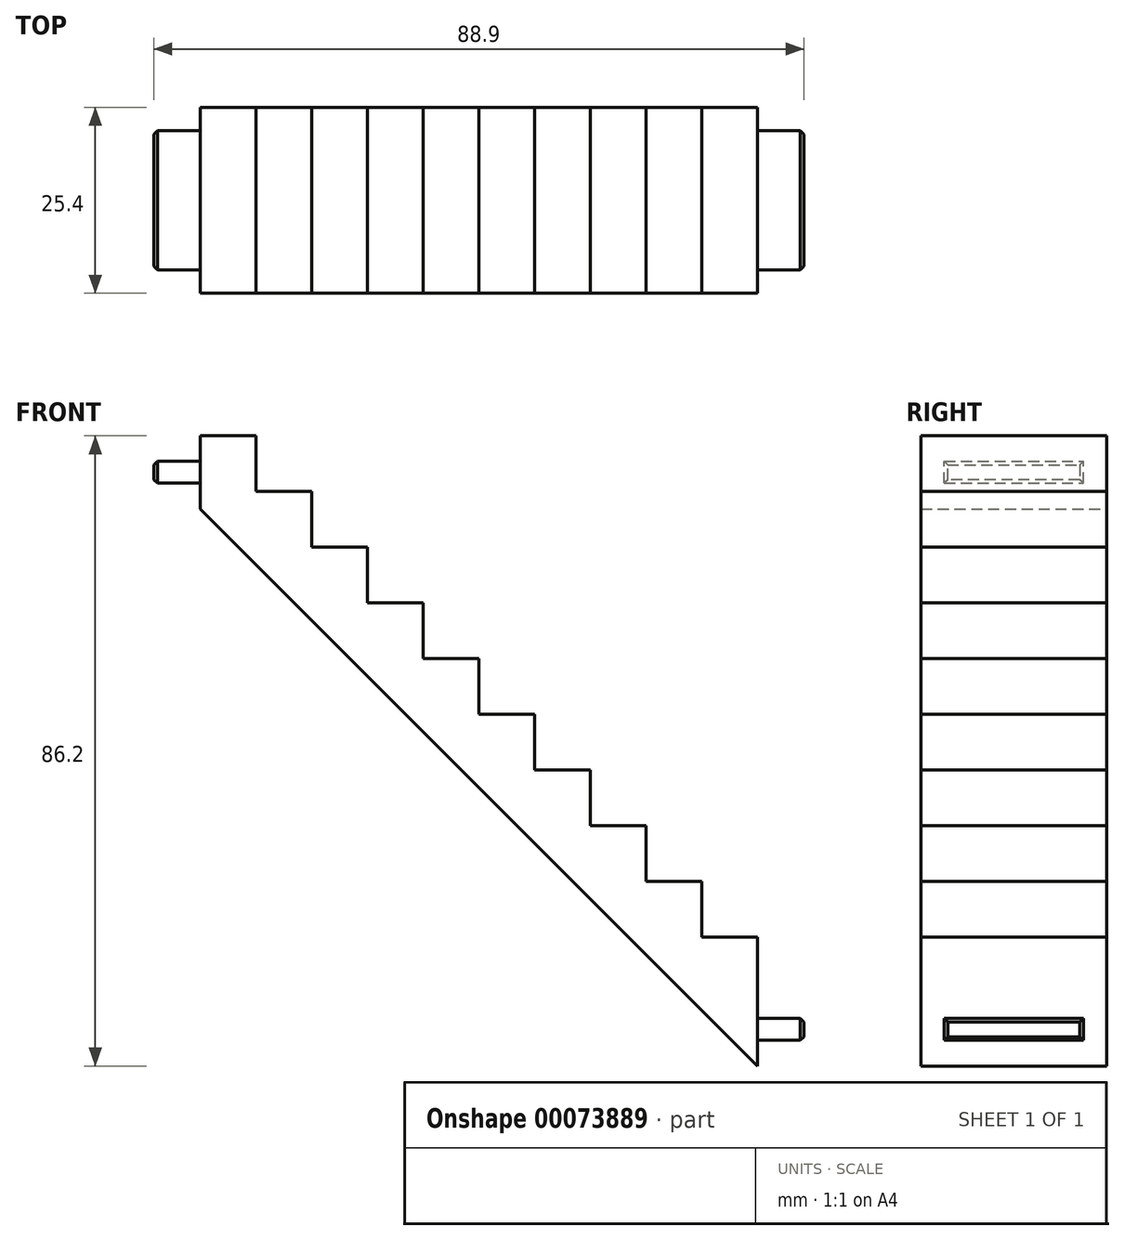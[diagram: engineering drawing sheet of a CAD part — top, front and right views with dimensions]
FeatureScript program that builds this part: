
annotation { "Feature Type Name" : "Feature", "Feature Type Description" : "" }
export const myFeature = defineFeature(function(context is Context, id is Id, definition is map)
    precondition{}
    {
        {
            var Q0;
            Q0=qCreatedBy(makeId("Front.planeOp"),FACE);
            var sketch = newSketch(context, id + "F0", { "sketchPlane" : qUnion([Q0])});
            skLineSegment(sketch, "E0.bottom", {"start": v(0, 0) * mm, "end": v(-76.2, 0) * mm, "construction": true});
            skLineSegment(sketch, "E0.top", {"start": v(0, 76.2) * mm, "end": v(-76.2, 76.2) * mm, "construction": true});
            skLineSegment(sketch, "E0.left", {"start": v(0, 0) * mm, "end": v(0, 76.2) * mm, "construction": true});
            skLineSegment(sketch, "E0.right", {"start": v(-76.2, 0) * mm, "end": v(-76.2, 76.2) * mm, "construction": true});
            skLineSegment(sketch, "E1", {"start": v(-76.2, 76.2) * mm, "end": v(0, 0) * mm, "construction": true});
            skLineSegment(sketch, "E2", {"start": v(0, 0) * mm, "end": v(0, -10) * mm});
            skLineSegment(sketch, "E3", {"start": v(-76.2, 76.2) * mm, "end": v(-76.2, 66.2) * mm});
            skLineSegment(sketch, "E4", {"start": v(-76.2, 66.2) * mm, "end": v(0, -10) * mm});
            skLineSegment(sketch, "E5", {"start": v(0, -10) * mm, "end": v(0, 0) * mm});
            skLineSegment(sketch, "E6", {"start": v(0, 0) * mm, "end": v(0, 7.62) * mm});
            skLineSegment(sketch, "E7", {"start": v(0, 7.62) * mm, "end": v(-7.62, 7.62) * mm});
            skLineSegment(sketch, "E8", {"start": v(-7.62, 7.62) * mm, "end": v(-7.62, 15.24) * mm});
            skLineSegment(sketch, "E9", {"start": v(-7.62, 15.24) * mm, "end": v(-15.24, 15.24) * mm});
            skLineSegment(sketch, "E10", {"start": v(-15.24, 15.24) * mm, "end": v(-15.24, 22.86) * mm});
            skLineSegment(sketch, "E11", {"start": v(-15.24, 22.86) * mm, "end": v(-22.86, 22.86) * mm});
            skLineSegment(sketch, "E12", {"start": v(-22.86, 22.86) * mm, "end": v(-22.86, 30.48) * mm});
            skLineSegment(sketch, "E13", {"start": v(-22.86, 30.48) * mm, "end": v(-30.48, 30.48) * mm});
            skLineSegment(sketch, "E14", {"start": v(-30.48, 30.48) * mm, "end": v(-30.48, 38.1) * mm});
            skLineSegment(sketch, "E15", {"start": v(-30.48, 38.1) * mm, "end": v(-38.1, 38.1) * mm});
            skLineSegment(sketch, "E16", {"start": v(-38.1, 38.1) * mm, "end": v(-38.1, 45.72) * mm});
            skLineSegment(sketch, "E17", {"start": v(-38.1, 45.72) * mm, "end": v(-45.72, 45.72) * mm});
            skLineSegment(sketch, "E18", {"start": v(-45.72, 45.72) * mm, "end": v(-45.72, 53.34) * mm});
            skLineSegment(sketch, "E19", {"start": v(-45.72, 53.34) * mm, "end": v(-53.34, 53.34) * mm});
            skLineSegment(sketch, "E20", {"start": v(-53.34, 53.34) * mm, "end": v(-53.34, 60.96) * mm});
            skLineSegment(sketch, "E21", {"start": v(-53.34, 60.96) * mm, "end": v(-60.96, 60.96) * mm});
            skLineSegment(sketch, "E22", {"start": v(-60.96, 60.96) * mm, "end": v(-60.96, 68.58) * mm});
            skLineSegment(sketch, "E23", {"start": v(-60.96, 68.58) * mm, "end": v(-68.58, 68.58) * mm});
            skLineSegment(sketch, "E24", {"start": v(-68.58, 68.58) * mm, "end": v(-68.58, 76.2) * mm});
            skLineSegment(sketch, "E25", {"start": v(-68.58, 76.2) * mm, "end": v(-76.2, 76.2) * mm});
            skSolve(sketch);
        }
        {
            var Q0;
            Q0=makeQuery(id+"F0.imprint","IMPRINT",FACE,{"disambiguationData":[TD([[makeQuery(id+"F0.imprint","IMPRINT",EDGE,{"derivedFrom":sQuery(id+"F0.wireOp",EDGE,"E3")}),1.0]])]});
            extrude(context, id + "F1", {"entities" : qUnion([Q0]), "endBound" : BoundingType.SYMMETRIC, "depth" : 25.4 * mm});
        }
        {
            var Q0;
            Q0=makeQuery(id+"F1.opExtrude","SWEPT_FACE",FACE,{"disambiguationData":[OSD([sQuery(id+"F0.wireOp",EDGE,"E5"),sQuery(id+"F0.wireOp",EDGE,"E6")])]});
            var sketch = newSketch(context, id + "F2", { "sketchPlane" : qUnion([Q0])});
            skLineSegment(sketch, "E26.bottom", {"start": v(-12.7, -10) * mm, "end": v(12.7, -10) * mm, "construction": true});
            skLineSegment(sketch, "E26.top", {"start": v(-12.7, 0) * mm, "end": v(12.7, 0) * mm, "construction": true});
            skLineSegment(sketch, "E26.left", {"start": v(-12.7, -10) * mm, "end": v(-12.7, 0) * mm, "construction": true});
            skLineSegment(sketch, "E26.right", {"start": v(12.7, -10) * mm, "end": v(12.7, 0) * mm, "construction": true});
            skPoint(sketch, "E26.middle", {"position": v(0, -5) * mm});
            skLineSegment(sketch, "E27.bottom", {"start": v(9.52, -6.5) * mm, "end": v(-9.53, -6.5) * mm});
            skLineSegment(sketch, "E27.top", {"start": v(9.53, -3.5) * mm, "end": v(-9.53, -3.5) * mm});
            skLineSegment(sketch, "E27.left", {"start": v(9.52, -6.5) * mm, "end": v(9.52, -3.5) * mm});
            skLineSegment(sketch, "E27.right", {"start": v(-9.53, -6.5) * mm, "end": v(-9.53, -3.5) * mm});
            skSolve(sketch);
        }
        {
            var Q0;
            Q0=makeQuery(id+"F2.imprint","IMPRINT",FACE,{"disambiguationData":[TD([[makeQuery(id+"F2.imprint","IMPRINT",EDGE,{"derivedFrom":sQuery(id+"F2.wireOp",EDGE,"E27.bottom")}),-1.0]])]});
            extrude(context, id + "F3", {"entities" : qUnion([Q0]), "operationType" : NewBodyOperationType.ADD, "depth" : 6.35 * mm});
        }
        {
            var Q0;
            Q0=makeQuery(id+"F1.opExtrude","SWEPT_FACE",FACE,{"disambiguationData":[OSD([sQuery(id+"F0.wireOp",EDGE,"E3")])]});
            var sketch = newSketch(context, id + "F4", { "sketchPlane" : qUnion([Q0])});
            skLineSegment(sketch, "E28.bottom", {"start": v(9.53, 69.7) * mm, "end": v(-9.53, 69.7) * mm});
            skLineSegment(sketch, "E28.top", {"start": v(9.53, 72.7) * mm, "end": v(-9.53, 72.7) * mm});
            skLineSegment(sketch, "E28.left", {"start": v(9.53, 69.7) * mm, "end": v(9.53, 72.7) * mm});
            skLineSegment(sketch, "E28.right", {"start": v(-9.53, 69.7) * mm, "end": v(-9.53, 72.7) * mm});
            skPoint(sketch, "E28.middle", {"position": v(0, 71.2) * mm});
            skPoint(sketch, "E28.middle.positionSnap0", {"position": v(-12.7, 71.2) * mm});
            skPoint(sketch, "E28.centerSnap0", {"position": v(-12.7, 71.2) * mm});
            skSolve(sketch);
        }
        {
            var Q0;
            Q0=makeQuery(id+"F4.imprint","IMPRINT",FACE,{"disambiguationData":[TD([[makeQuery(id+"F4.imprint","IMPRINT",EDGE,{"derivedFrom":sQuery(id+"F4.wireOp",EDGE,"E28.bottom")}),-1.0]])]});
            extrude(context, id + "F5", {"entities" : qUnion([Q0]), "operationType" : NewBodyOperationType.ADD, "depth" : 6.35 * mm});
        }
        {
            var Q0;
            Q0=makeQuery(id+"F5.opExtrude","CAP_EDGE",EDGE,{"disambiguationData":[OSD([sQuery(id+"F4.wireOp",EDGE,"E28.top")])],"isStart":false});
            var Q1;
            Q1=makeQuery(id+"F5.opExtrude","CAP_EDGE",EDGE,{"disambiguationData":[OSD([sQuery(id+"F4.wireOp",EDGE,"E28.right")])],"isStart":false});
            var Q2;
            Q2=makeQuery(id+"F5.opExtrude","CAP_EDGE",EDGE,{"disambiguationData":[OSD([sQuery(id+"F4.wireOp",EDGE,"E28.bottom")])],"isStart":false});
            var Q3;
            Q3=makeQuery(id+"F5.opExtrude","CAP_EDGE",EDGE,{"disambiguationData":[OSD([sQuery(id+"F4.wireOp",EDGE,"E28.left")])],"isStart":false});
            var Q4;
            Q4=makeQuery(id+"F3.opExtrude","CAP_EDGE",EDGE,{"disambiguationData":[OSD([sQuery(id+"F2.wireOp",EDGE,"E27.left")])],"isStart":false});
            var Q5;
            Q5=makeQuery(id+"F3.opExtrude","CAP_EDGE",EDGE,{"disambiguationData":[OSD([sQuery(id+"F2.wireOp",EDGE,"E27.top")])],"isStart":false});
            var Q6;
            Q6=makeQuery(id+"F3.opExtrude","CAP_EDGE",EDGE,{"disambiguationData":[OSD([sQuery(id+"F2.wireOp",EDGE,"E27.right")])],"isStart":false});
            var Q7;
            Q7=makeQuery(id+"F3.opExtrude","CAP_EDGE",EDGE,{"disambiguationData":[OSD([sQuery(id+"F2.wireOp",EDGE,"E27.bottom")])],"isStart":false});
            chamfer(context, id + "F6", {"entities" : qUnion([Q0, Q1, Q2, Q3, Q4, Q5, Q6, Q7]), "width" : 0.5 * mm});
        }
        {
            var Q0;
            Q0=makeQuery(id+"F1.opExtrude","SWEPT_FACE",FACE,{"disambiguationData":[OSD([sQuery(id+"F0.wireOp",EDGE,"E5"),sQuery(id+"F0.wireOp",EDGE,"E6")])]});
            var sketch = newSketch(context, id + "F7", { "sketchPlane" : qUnion([Q0])});
            skLineSegment(sketch, "E29.bottom", {"start": v(12.7, -10) * mm, "end": v(-12.7, -10) * mm});
            skLineSegment(sketch, "E29.top", {"start": v(12.7, 0) * mm, "end": v(-12.7, 0) * mm});
            skLineSegment(sketch, "E29.left", {"start": v(12.7, -10) * mm, "end": v(12.7, 0) * mm});
            skLineSegment(sketch, "E29.right", {"start": v(-12.7, -10) * mm, "end": v(-12.7, 0) * mm});
            skPoint(sketch, "E29.middle", {"position": v(0, -5) * mm});
            skPoint(sketch, "E29.middle.positionSnap0", {"position": v(9.52, -5) * mm});
            skPoint(sketch, "E29.middle.positionSnap1", {"position": v(0, -6.5) * mm});
            skPoint(sketch, "E29.centerSnap0", {"position": v(9.52, -5) * mm});
            skPoint(sketch, "E29.centerSnap1", {"position": v(0, -6.5) * mm});
            skSolve(sketch);
        }
    });
